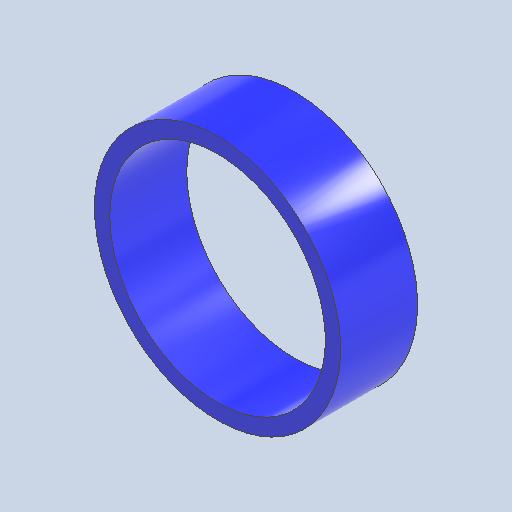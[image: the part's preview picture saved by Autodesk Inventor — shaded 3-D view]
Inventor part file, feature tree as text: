
AUTODESK INVENTOR PART (.ipt)
format: ipt  version: 2022 (Build 260153000, 153)  size: 115,200 bytes
history: imported  units: in
note: dims shown in document units (in); Inventor stores cm internally (conversion verified against a paired STEP export)
features: imported_body x1
ambient origin geometry x8: Origin, YZ Plane, XZ Plane, XY Plane, X Axis, Y Axis, Z Axis, Center Point
bodies: Solid1 (imported_parasolid), Body1 (imported_parasolid)
feature tree (1):
  imported_body  NMx_Import_Brep_tag  [imported B-rep: ~4 faces, bbox_mm=[1.0, 0.0, 5.0]]
